# Revit family: Haworth_BuzziMoon_Light
name_source: partatom
category: Lighting Fixtures
revit_build: Autodesk Revit 2018 (Build: 20170223_1515(x64)
units: mm (PartAtom-declared; Revit-internal decimal feet)

## family parameters
Cut with Voids When Loaded = No
Host = Face
Light Source = Yes
Part Type = Normal
Room Calculation Point = No
Round Connector Dimension = Use Diameter
Shared = No

## types (3) — shared parameters
3D Drop = No
3D Leaf = Yes
3D Rib = No
Actual Height = 2.36 "
Assembly Code = E2020200
Color Filter = 16777215
Cords Finish = Haworth _ Paint _ Collection White
Dimming Lamp Color Temperature Shift = <None>
Emit Shape Visible in Rendering = No
Emit from Circle Diameter = 20 "
Flat = No
Glass Finish = Haworth _ Glass _ Frosted
Manufacturer = Haworth
Max. Cable Length = 157.48 "
Min. Cable Length = 15 "
Model = HCBZ-MNP
Note = Verify Final Dim. w/ Haworth
Photometric Web File = generic
Revision = 1
Three Cable Length = 10 "
Tilt Angle = 90.00°
URL = http://www.haworth.com
URL - Product = https://www.haworth.com
Warranty = http://www.haworth.com
zero-valued in all types: Default Elevation

## per-type parameters (varying)
| type | Actual Depth | Actual Width | Description | Large | Medium | Small |
| HCBZ-MNP3 - Large | 47.24 " | 47.24 " | Haworth BuzziMoon Pendant Light Large | Yes | No | No |
| HCBZ-MNP2 - Medium | 39.37 " | 39.37 " | Haworth BuzziMoon Pendant Light Medium | No | Yes | No |
| HCBZ-MNP1 - Small | 31.5 " | 31.5 " | Haworth BuzziMoon Pendant Light Small | No | No | Yes |

## geometry (parser evidence)
native form markers: Sweep x7
no freeform markers — native parametric forms only
